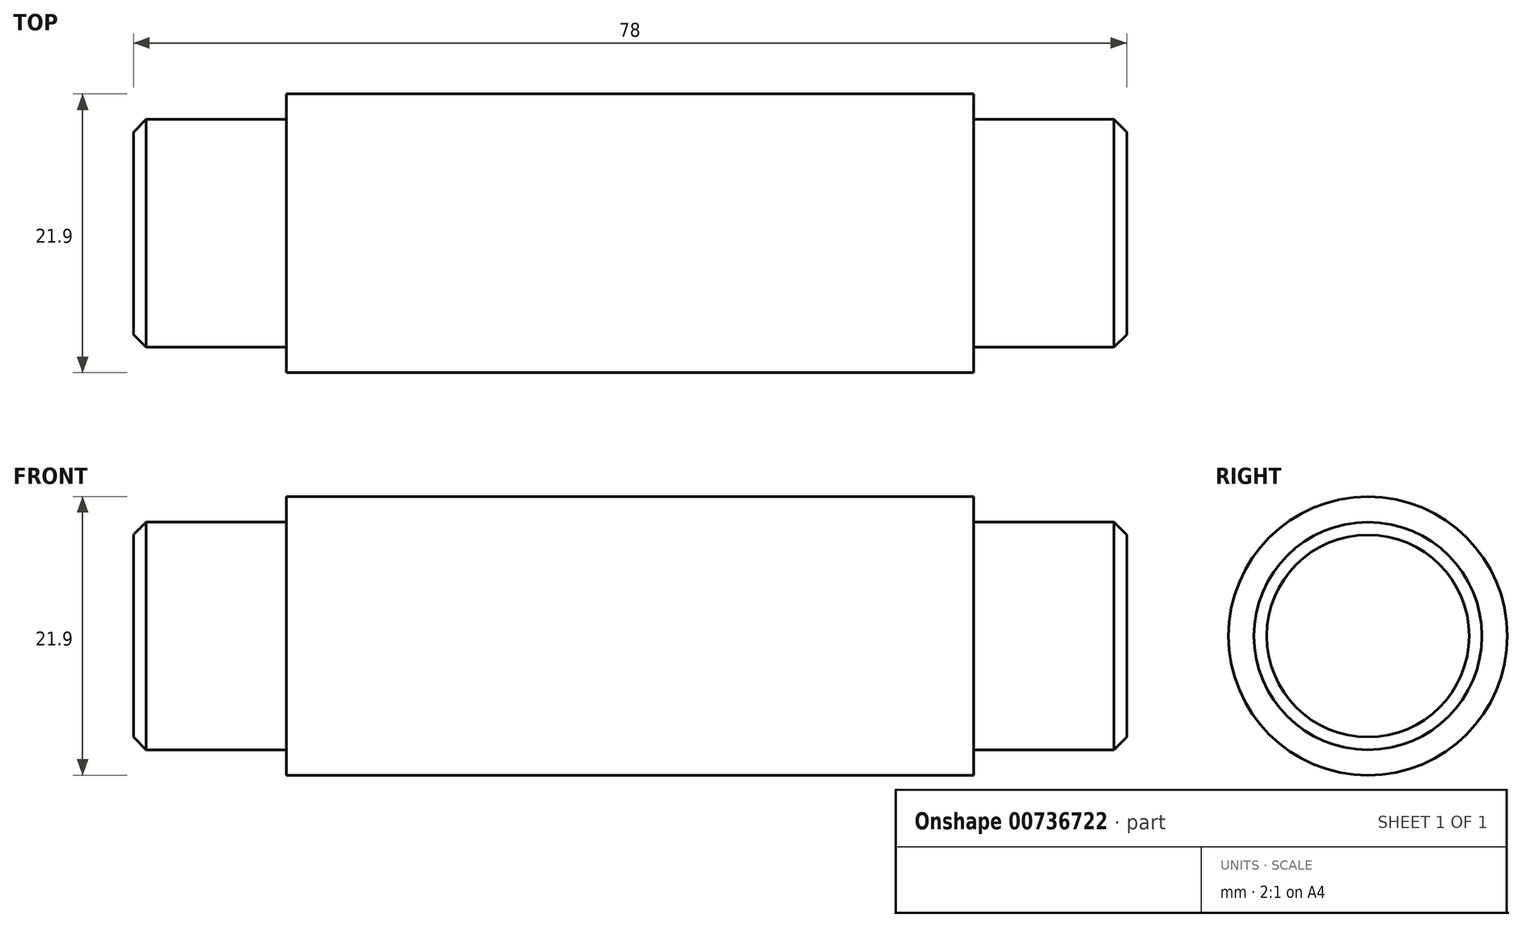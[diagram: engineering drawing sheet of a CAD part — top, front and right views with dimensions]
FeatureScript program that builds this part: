
annotation { "Feature Type Name" : "Feature", "Feature Type Description" : "" }
export const myFeature = defineFeature(function(context is Context, id is Id, definition is map)
    precondition{}
    {
        {
            var Q0;
            Q0=qCreatedBy(makeId("Right.planeOp"),FACE);
            var sketch = newSketch(context, id + "F0", { "sketchPlane" : qUnion([Q0])});
            skCircle(sketch, "E0", {"center": v(0, 0) * mm, "radius": 10.95 * mm});
            skSolve(sketch);
        }
        {
            var Q0;
            Q0=makeQuery(id+"F0.imprint","IMPRINT",FACE,{"disambiguationData":[TD([[makeQuery(id+"F0.imprint","IMPRINT",EDGE,{"derivedFrom":sQuery(id+"F0.wireOp",EDGE,"E0")}),1.0]])]});
            extrude(context, id + "F1", {"entities" : qUnion([Q0]), "depth" : 27 * mm, "offsetDistance" : 25 * mm, "hasSecondDirection" : true, "secondDirectionOppositeDirection" : true, "secondDirectionDepth" : 27 * mm});
        }
        {
            var Q0;
            Q0=makeQuery(id+"F1.opExtrude","CAP_FACE",FACE,{"disambiguationData":[OSD([sQuery(id+"F0.wireOp",EDGE,"E0")])],"isStart":false});
            var sketch = newSketch(context, id + "F2", { "sketchPlane" : qUnion([Q0])});
            skCircle(sketch, "E1", {"center": v(0, 0) * mm, "radius": 8.95 * mm});
            skSolve(sketch);
        }
        {
            var Q0;
            Q0=makeQuery(id+"F2.imprint","IMPRINT",FACE,{"disambiguationData":[TD([[makeQuery(id+"F2.imprint","IMPRINT",EDGE,{"derivedFrom":sQuery(id+"F2.wireOp",EDGE,"E1")}),1.0]])]});
            extrude(context, id + "F3", {"entities" : qUnion([Q0]), "operationType" : NewBodyOperationType.ADD, "depth" : 12 * mm, "offsetDistance" : 25 * mm});
        }
        {
            var Q0;
            Q0=makeQuery(id+"F3.opExtrude","CAP_EDGE",EDGE,{"disambiguationData":[OSD([sQuery(id+"F2.wireOp",EDGE,"E1")])],"isStart":false});
            chamfer(context, id + "F4", {"entities" : qUnion([Q0]), "width" : 1 * mm, "tangentPropagation" : true});
        }
        {
            var Q0;
            Q0=makeQuery(id+"F1.opExtrude","CAP_FACE",FACE,{"disambiguationData":[OSD([sQuery(id+"F0.wireOp",EDGE,"E0")])],"isStart":true});
            var sketch = newSketch(context, id + "F5", { "sketchPlane" : qUnion([Q0])});
            skCircle(sketch, "E2", {"center": v(0, 0) * mm, "radius": 8.95 * mm});
            skSolve(sketch);
        }
        {
            var Q0;
            Q0 = qSketchRegion(id + "F5", true);
            extrude(context, id + "F6", {"entities" : qUnion([Q0]), "operationType" : NewBodyOperationType.ADD, "depth" : 12 * mm, "offsetDistance" : 25 * mm});
        }
        {
            var Q0;
            Q0=makeQuery(id+"F6.opExtrude","CAP_EDGE",EDGE,{"disambiguationData":[OSD([sQuery(id+"F5.wireOp",EDGE,"E2")])],"isStart":false});
            chamfer(context, id + "F7", {"entities" : qUnion([Q0]), "width" : 1 * mm, "tangentPropagation" : true});
        }
    });
